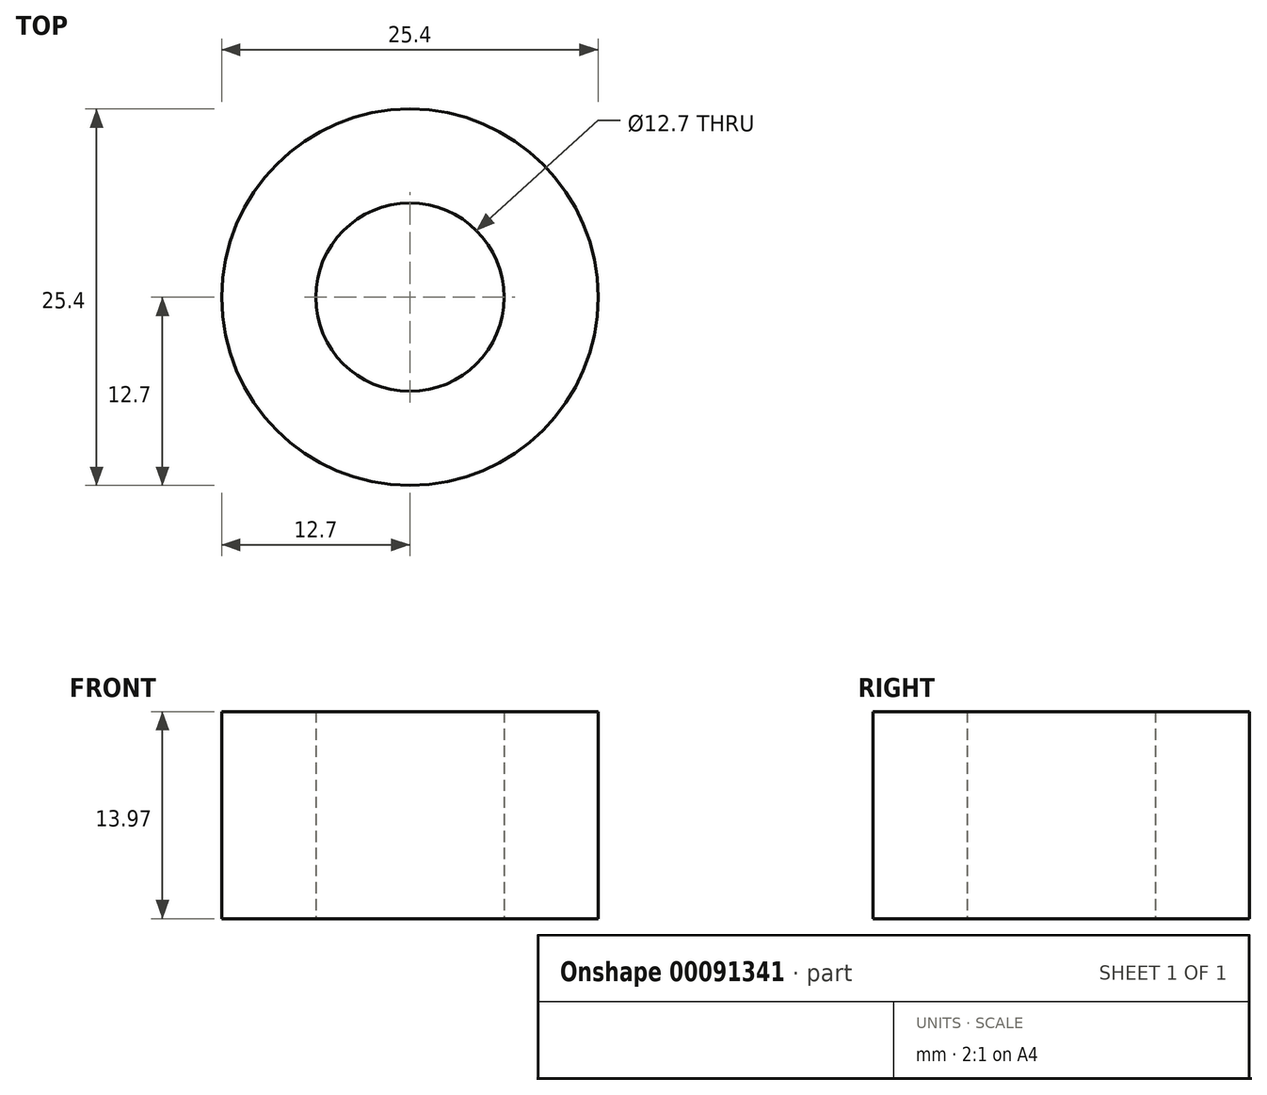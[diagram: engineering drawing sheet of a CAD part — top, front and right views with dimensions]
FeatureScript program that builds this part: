
annotation { "Feature Type Name" : "Feature", "Feature Type Description" : "" }
export const myFeature = defineFeature(function(context is Context, id is Id, definition is map)
    precondition{}
    {
        {
            var Q0;
            Q0=qCreatedBy(makeId("Top.planeOp"),FACE);
            var sketch = newSketch(context, id + "F0", { "sketchPlane" : qUnion([Q0])});
            skCircle(sketch, "E0", {"center": v(0, 0) * mm, "radius": 6.35 * mm});
            skCircle(sketch, "E1", {"center": v(0, 0) * mm, "radius": 12.7 * mm});
            skSolve(sketch);
        }
        {
            var Q0;
            Q0=makeQuery(id+"F0.imprint","IMPRINT",FACE,{"disambiguationData":[TD([[makeQuery(id+"F0.imprint","IMPRINT",EDGE,{"derivedFrom":sQuery(id+"F0.wireOp",EDGE,"E0")}),-1.0]])]});
            extrude(context, id + "F1", {"entities" : qUnion([Q0]), "depth" : 13.97 * mm});
        }
    });
